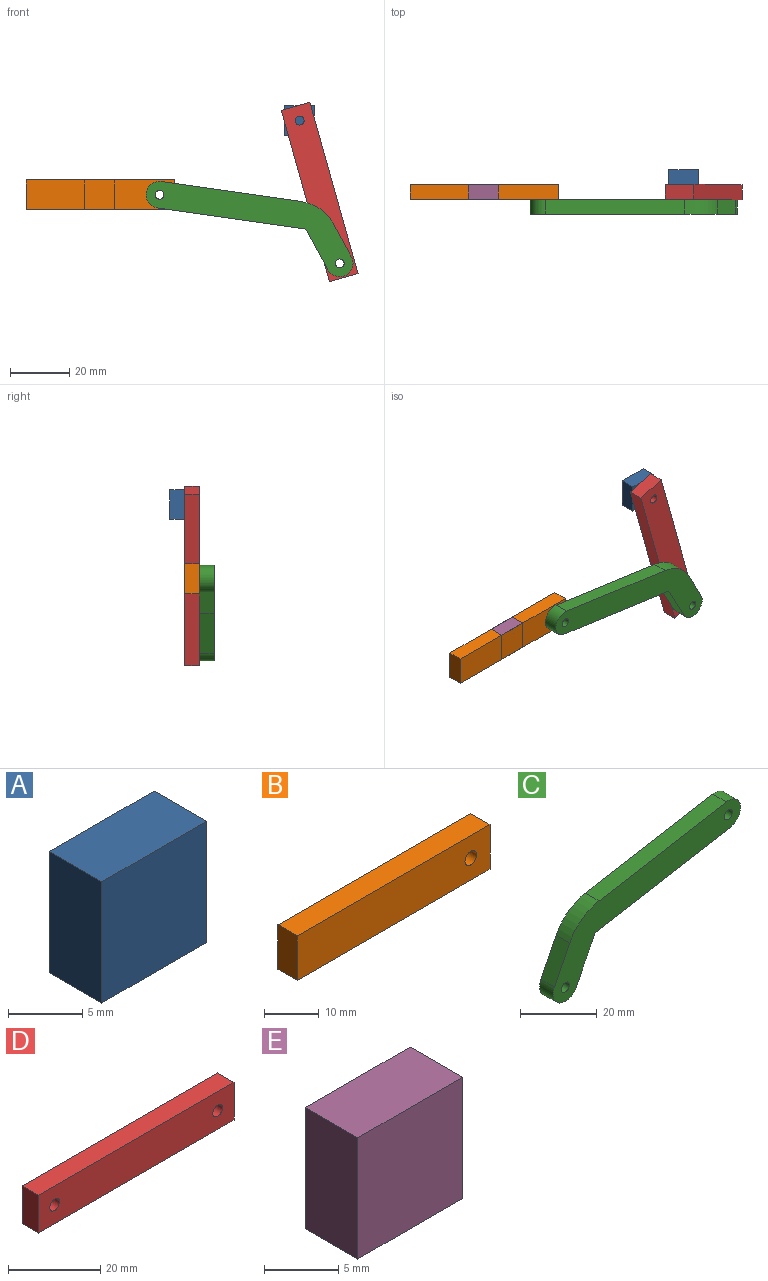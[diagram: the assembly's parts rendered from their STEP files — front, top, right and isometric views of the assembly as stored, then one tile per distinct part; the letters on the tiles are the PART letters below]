
ASSEMBLY  parts=5 mates=4
PART A: 6 faces, bbox 10x5x10 mm
  f0: plane 10x5mm, normal (0,0,-1), area 50mm2, adj f1,f3,f4,f5
  f1: plane 10x5mm, normal (-1,0,0), area 50mm2, adj f0,f2,f4,f5
  f2: plane 10x5mm, normal (0,0,1), area 50mm2, adj f1,f3,f4,f5
  f3: plane 10x5mm, normal (1,0,0), area 50mm2, adj f0,f2,f4,f5
  f4: plane 10x10mm, normal (0,1,0), area 100mm2, adj f0,f1,f2,f3
  f5: plane 10x10mm, normal (0,-1,0), area 100mm2, adj f0,f1,f2,f3
PART B: 7 faces, bbox 50x5x10 mm
  f0: plane 10x5mm, normal (1,0,0), area 50mm2, adj f1,f4,f5,f6
  f1: plane 50x5mm, normal (0,0,1), area 250mm2, adj f0,f2,f5,f6
  f2: plane 10x5mm, normal (-1,0,0), area 50mm2, adj f1,f4,f5,f6
  f3: cylinder r=1.5mm len=5mm, axis (0,-1,0), area 47.1mm2, adj f5,f6
  f4: plane 50x5mm, normal (0,0,-1), area 250mm2, adj f0,f2,f5,f6
  f5: plane 50x10mm, normal (0,1,0), area 492.9mm2, adj f0,f1,f2,f3,f4
  f6: plane 50x10mm, normal (0,-1,0), area 492.9mm2, adj f0,f1,f2,f3,f4
PART C: 11 faces, bbox 69x5x34 mm
  f0: plane 13.93x6.99mm, normal (0.89,0,-0.45), area 77.9mm2, adj f1,f7,f9,f10
  f1: plane 49.76x8.66mm, normal (0.17,0,-0.99), area 252.5mm2, adj f0,f2,f9,f10
  f2: cylinder r=4.5mm len=8.93mm, axis (0,1,0), area 70.7mm2, adj f1,f3,f9,f10
  f3: plane 46.78x8.14mm, normal (-0.17,0,0.99), area 237.4mm2, adj f2,f4,f9,f10
  f4: cylinder r=15mm len=10.84mm, axis (0,1,0), area 70mm2, adj f3,f5,f9,f10
  f5: plane 11.23x5.63mm, normal (-0.89,0,0.45), area 62.8mm2, adj f4,f7,f9,f10
  f6: cylinder r=1.5mm len=5mm, axis (0,1,0), area 47.1mm2, adj f9,f10
  f7: cylinder r=4.5mm len=8.52mm, axis (0,1,0), area 70.7mm2, adj f0,f5,f9,f10
  f8: cylinder r=1.5mm len=5mm, axis (0,1,0), area 47.1mm2, adj f9,f10
  f9: plane 69x34mm, normal (0,-1,0), area 676.8mm2, adj f0,f1,f2,f3,f4,f5,f6,f7
  f10: plane 69x34mm, normal (0,1,0), area 676.8mm2, adj f0,f1,f2,f3,f4,f5,f6,f7
PART D: 8 faces, bbox 60x5x10 mm
  f0: plane 10x5mm, normal (-1,0,0), area 50mm2, adj f1,f4,f6,f7
  f1: plane 60x5mm, normal (0,0,-1), area 300mm2, adj f0,f2,f6,f7
  f2: plane 10x5mm, normal (1,0,0), area 50mm2, adj f1,f4,f6,f7
  f3: cylinder r=1.5mm len=5mm, axis (0,-1,0), area 47.1mm2, adj f6,f7
  f4: plane 60x5mm, normal (0,0,1), area 300mm2, adj f0,f2,f6,f7
  f5: cylinder r=1.5mm len=5mm, axis (0,-1,0), area 47.1mm2, adj f6,f7
  f6: plane 60x10mm, normal (0,1,0), area 585.9mm2, adj f0,f1,f2,f3,f4,f5
  f7: plane 60x10mm, normal (0,-1,0), area 585.9mm2, adj f0,f1,f2,f3,f4,f5
PART E: 6 faces, bbox 10x5x10 mm
  f0: plane 10x5mm, normal (1,0,0), area 50mm2, adj f1,f3,f4,f5
  f1: plane 10x5mm, normal (0,0,1), area 50mm2, adj f0,f2,f4,f5
  f2: plane 10x5mm, normal (-1,0,0), area 50mm2, adj f1,f3,f4,f5
  f3: plane 10x5mm, normal (0,0,-1), area 50mm2, adj f0,f2,f4,f5
  f4: plane 10x10mm, normal (0,1,0), area 100mm2, adj f0,f1,f2,f3
  f5: plane 10x10mm, normal (0,-1,0), area 100mm2, adj f0,f1,f2,f3
PLACE A t=(-20.98,21.78,-6.64)mm fixed
PLACE B rot(axis=(-1,0,0),0deg) t=(-58.2,21.78,-6.64)mm
PLACE C rot(axis=(0.02,0,-1),180deg) t=(42.53,11.78,-29.17)mm
PLACE D rot(axis=(0,1,0),74.3deg) t=(-23.15,21.78,40.48)mm
PLACE E t=(-13.49,21.78,-6.64)mm fixed
MATE pin_slot B.f6 <-> E.f5  axis (0,-1,0) through (-58.49,21.78,-6.64)mm
MATE revolute D.f5 <-> C.f6  axis (0,-1,0) through (22.54,21.78,-29.78)mm
MATE revolute C.f2 <-> B.f3  axis (0,1,0) through (-38.2,21.78,-6.64)mm
MATE revolute D.f3 <-> A.f5  axis (0,1,0) through (9.02,26.78,18.36)mm
